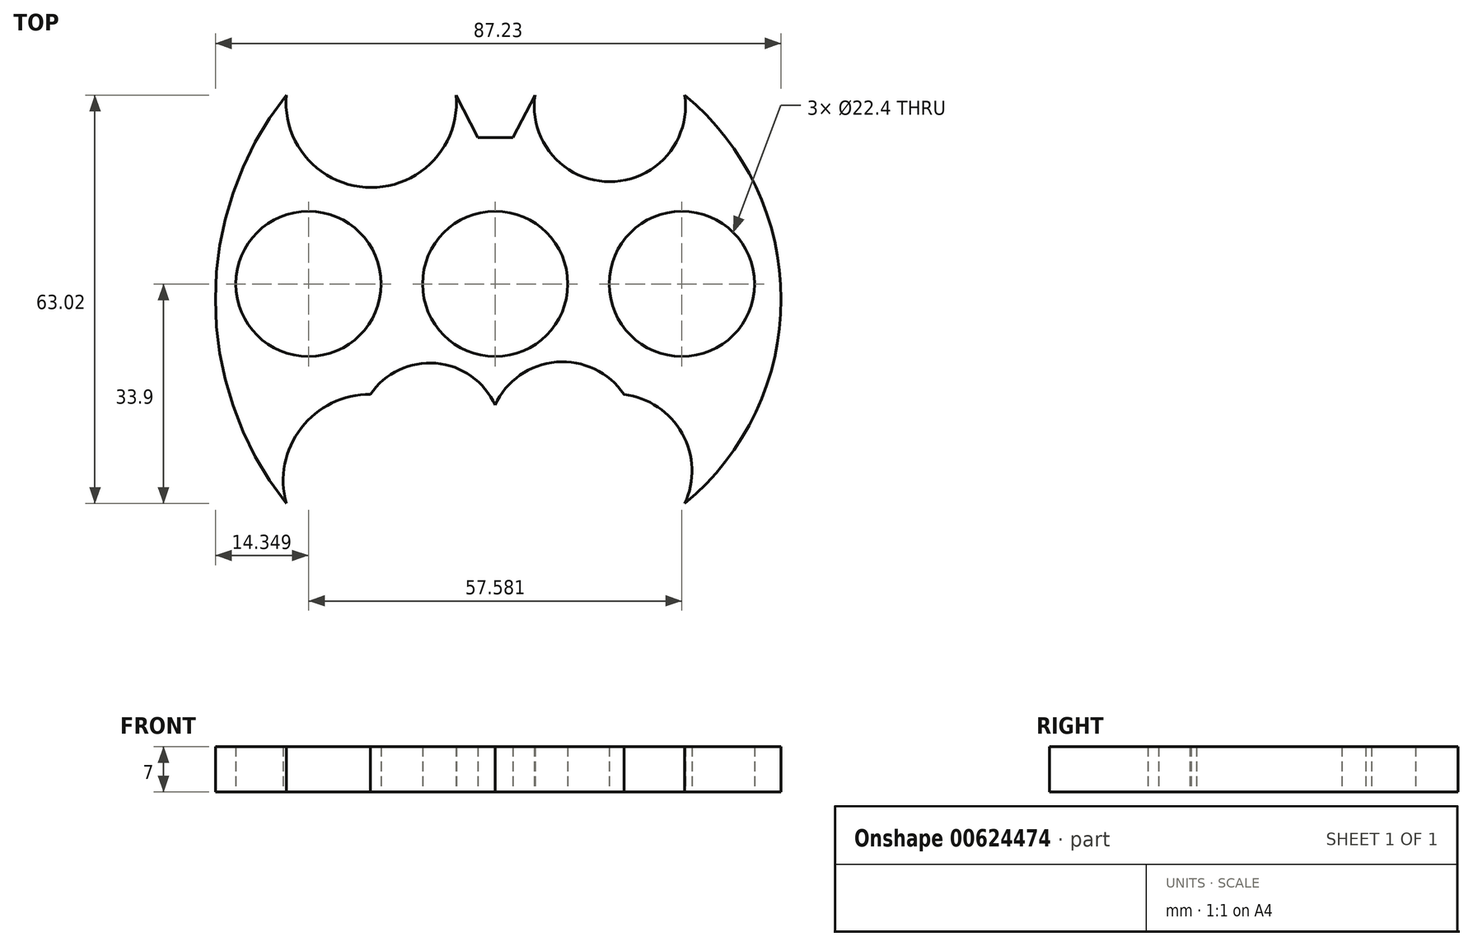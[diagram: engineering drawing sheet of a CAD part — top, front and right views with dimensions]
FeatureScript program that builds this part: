
annotation { "Feature Type Name" : "Feature", "Feature Type Description" : "" }
export const myFeature = defineFeature(function(context is Context, id is Id, definition is map)
    precondition{}
    {
        {
            var Q0;
            Q0=qCreatedBy(makeId("Top.planeOp"),FACE);
            var sketch = newSketch(context, id + "F0", { "sketchPlane" : qUnion([Q0])});
            skCircle(sketch, "E0", {"center": v(0, 0) * mm, "radius": 11.2 * mm});
            skArc(sketch, "E1", {"start": v(0, -18.71) * mm, "mid": v(-9.13, -12.24) * mm, "end": v(-19.24, -17.06) * mm});
            skArc(sketch, "E2", {"start": v(-19.24, -17.06) * mm, "mid": v(-29.92, -22.25) * mm, "end": v(-32.22, -33.9) * mm});
            skArc(sketch, "E3", {"start": v(-32.22, 29.12) * mm, "mid": v(-19.11, 14.87) * mm, "end": v(-6, 29.12) * mm});
            skArc(sketch, "E4", {"start": v(19.85, -17.06) * mm, "mid": v(9.44, -12.05) * mm, "end": v(0, -18.71) * mm});
            skArc(sketch, "E5", {"start": v(29.22, -33.9) * mm, "mid": v(28.84, -23.09) * mm, "end": v(19.85, -17.06) * mm});
            skArc(sketch, "E6", {"start": v(-32.22, 29.12) * mm, "mid": v(-43.14, -2.39) * mm, "end": v(-32.22, -33.9) * mm});
            skArc(sketch, "E7", {"start": v(6.13, 29.12) * mm, "mid": v(17.68, 15.78) * mm, "end": v(29.22, 29.12) * mm});
            skArc(sketch, "E8", {"start": v(29.22, -33.9) * mm, "mid": v(44.09, -2.39) * mm, "end": v(29.22, 29.12) * mm});
            skLineSegment(sketch, "E9", {"start": v(6.13, 29.12) * mm, "end": v(2.73, 22.56) * mm});
            skLineSegment(sketch, "E10", {"start": v(-2.65, 22.56) * mm, "end": v(-6, 29.12) * mm});
            skLineSegment(sketch, "E11", {"start": v(-2.65, 22.56) * mm, "end": v(2.73, 22.56) * mm});
            skCircle(sketch, "E12", {"center": v(-28.8, 0) * mm, "radius": 11.2 * mm});
            skCircle(sketch, "E13.2.0", {"center": v(28.8, 0) * mm, "radius": 11.2 * mm});
            skLineSegment(sketch, "E13.anchor1", {"start": v(0, 0) * mm, "end": v(-28.8, 0) * mm, "construction": true});
            skLineSegment(sketch, "E13.anchor2", {"start": v(0, 0) * mm, "end": v(28.8, 0) * mm, "construction": true});
            skSolve(sketch);
        }
        {
            var Q0;
            {var subQ0=sQuery(id+"F0.wireOp",EDGE,"E3");var subQ1=sQuery(id+"F0.wireOp",EDGE,"wIcN4tQ4-OL0U-KsKI-jLEZ-Zv3lfoWd9Mhj");var subQ2=makeQuery(id+"F0.imprint","INTERSECT",VERTEX,{"disambiguationData":[OD(0.0)],"derivedFrom":[subQ1,subQ0]});Q0=makeQuery(id+"F0.imprint","IMPRINT",FACE,{"disambiguationData":[TD([[makeQuery(id+"F0.imprint","IMPRINT",EDGE,{"disambiguationData":[TD([[subQ2,-1.0]])],"derivedFrom":subQ1}),1.0]])]});}
            var Q1;
            {var subQ0=sQuery(id+"F0.wireOp",EDGE,"E7");var subQ1=sQuery(id+"F0.wireOp",EDGE,"uIxHRKaC-fXGP-C11L-FGjw-L1SI6bDexqCe");var subQ2=makeQuery(id+"F0.imprint","INTERSECT",VERTEX,{"disambiguationData":[OD(0.0)],"derivedFrom":[subQ1,subQ0]});Q1=makeQuery(id+"F0.imprint","IMPRINT",FACE,{"disambiguationData":[TD([[makeQuery(id+"F0.imprint","IMPRINT",EDGE,{"disambiguationData":[TD([[subQ2,1.0]])],"derivedFrom":subQ1}),1.0]])]});}
            var Q2;
            Q2=makeQuery(id+"F0.imprint","IMPRINT",FACE,{"disambiguationData":[TD([[makeQuery(id+"F0.imprint","IMPRINT",EDGE,{"derivedFrom":sQuery(id+"F0.wireOp",EDGE,"E0")}),-1.0]])]});
            extrude(context, id + "F1", {"entities" : qUnion([Q0, Q1, Q2]), "depth" : 7 * mm, "offsetDistance" : 25 * mm});
        }
    });
